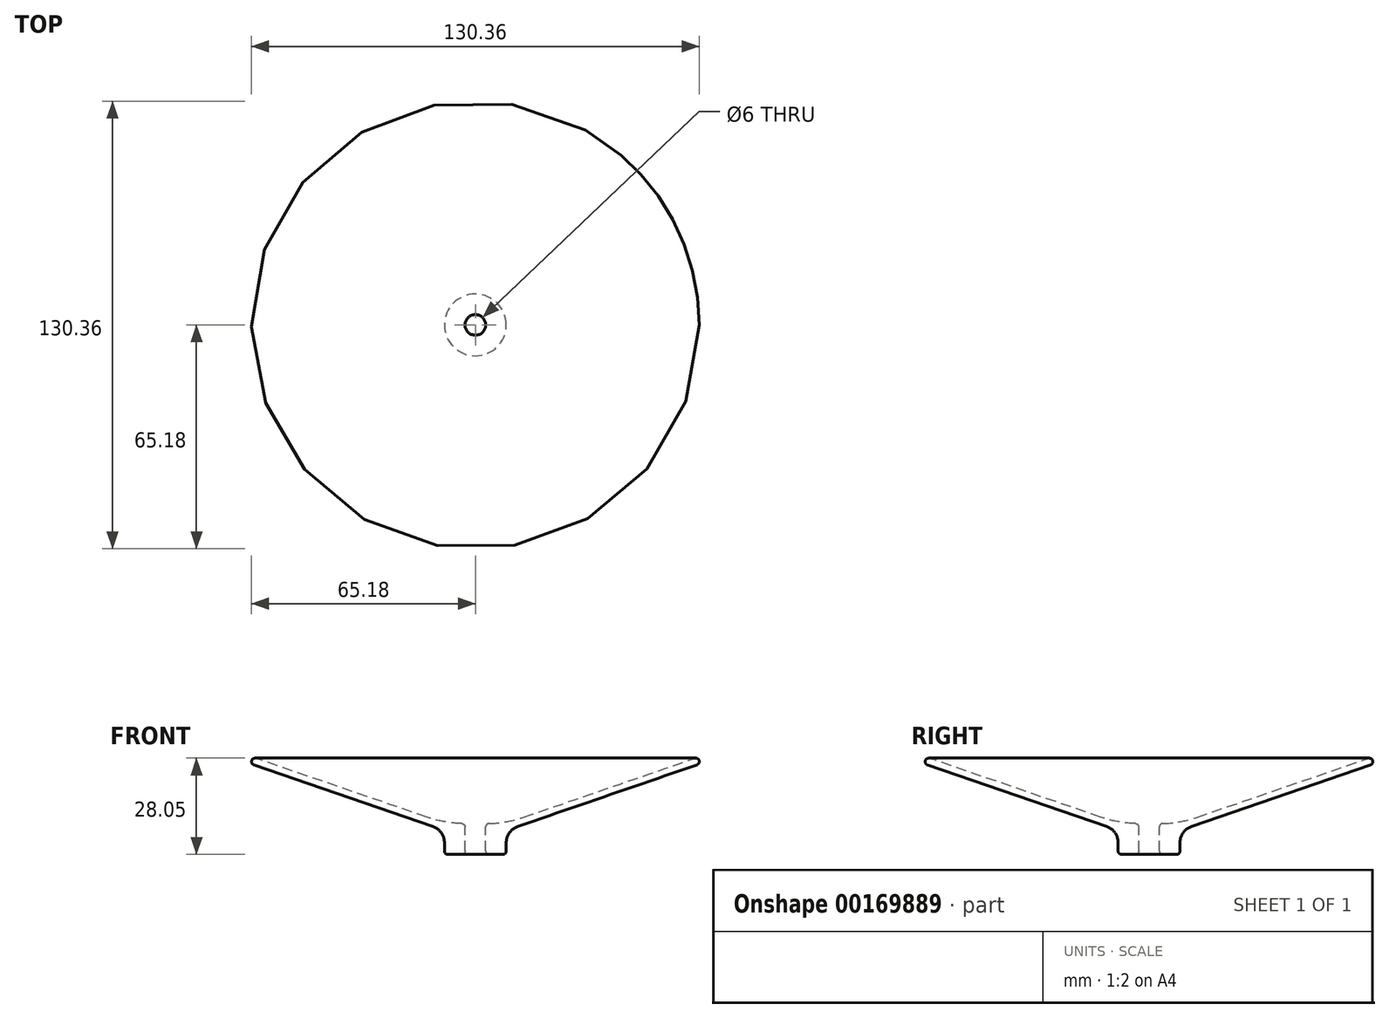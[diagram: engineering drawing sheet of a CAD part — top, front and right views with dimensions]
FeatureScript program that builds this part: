
annotation { "Feature Type Name" : "Feature", "Feature Type Description" : "" }
export const myFeature = defineFeature(function(context is Context, id is Id, definition is map)
    precondition{}
    {
        {
            var Q0;
            Q0=qCreatedBy(makeId("Right.planeOp"),FACE);
            var sketch = newSketch(context, id + "F0", { "sketchPlane" : qUnion([Q0])});
            skLineSegment(sketch, "E0", {"start": v(0, 28) * mm, "end": v(0, 0) * mm, "construction": true});
            skLineSegment(sketch, "E1", {"start": v(0, 0) * mm, "end": v(-9, 0) * mm, "construction": true});
            skLineSegment(sketch, "E2", {"start": v(0, 28) * mm, "end": v(-70, 28) * mm, "construction": true});
            skLineSegment(sketch, "E3", {"start": v(0, 3.93) * mm, "end": v(-3, 3.93) * mm, "construction": true});
            skLineSegment(sketch, "E4", {"start": v(-64.5, 26.1) * mm, "end": v(-12.37, 8.16) * mm});
            skLineSegment(sketch, "E5", {"start": v(-9, 3.43) * mm, "end": v(-9, 1) * mm});
            skLineSegment(sketch, "E6", {"start": v(-3, 1) * mm, "end": v(-3, 7.05) * mm});
            skLineSegment(sketch, "E7", {"start": v(-14.07, 10.86) * mm, "end": v(-63.86, 28) * mm});
            skPoint(sketch, "E8.visualSharp", {"position": v(-9, 7) * mm});
            skArc(sketch, "E8.filletArc", {"start": v(-9, 3.43) * mm, "mid": v(-9.93, 6.34) * mm, "end": v(-12.37, 8.16) * mm});
            skLineSegment(sketch, "E9", {"start": v(-8, 0) * mm, "end": v(-4, 0) * mm});
            skPoint(sketch, "E10.visualSharp", {"position": v(-9, 0) * mm});
            skArc(sketch, "E10.filletArc", {"start": v(-9, 1) * mm, "mid": v(-8.7, 0.3) * mm, "end": v(-8, 0) * mm});
            skPoint(sketch, "E11.visualSharp", {"position": v(-3, 0) * mm});
            skArc(sketch, "E11.filletArc", {"start": v(-4, 0) * mm, "mid": v(-3.3, 0.3) * mm, "end": v(-3, 1) * mm});
            skPoint(sketch, "E12", {"position": v(-14.07, 10.86) * mm});
            skLineSegment(sketch, "E13", {"start": v(-3, 7.05) * mm, "end": v(-3, 8.02) * mm});
            skArc(sketch, "E14", {"start": v(-14.07, 10.86) * mm, "mid": v(-9.1, 9.56) * mm, "end": v(-3.97, 9.02) * mm});
            skPoint(sketch, "E15.visualSharp", {"position": v(-3, 9) * mm});
            skArc(sketch, "E15.filletArc", {"start": v(-3, 8.02) * mm, "mid": v(-3.28, 8.71) * mm, "end": v(-3.97, 9.02) * mm});
            skLineSegment(sketch, "E16", {"start": v(-63.86, 28) * mm, "end": v(-63.86, 28) * mm});
            skPoint(sketch, "E17.visualSharp", {"position": v(-70, 28) * mm});
            skArc(sketch, "E17.filletArc", {"start": v(-63.86, 28) * mm, "mid": v(-65.13, 27.38) * mm, "end": v(-64.5, 26.1) * mm});
            skSolve(sketch);
        }
        {
            var Q0;
            Q0=makeQuery(id+"F0.imprint","IMPRINT",FACE,{"disambiguationData":[TD([[makeQuery(id+"F0.imprint","IMPRINT",EDGE,{"derivedFrom":sQuery(id+"F0.wireOp",EDGE,"E4")}),1.0]])]});
            var Q1;
            Q1=sQuery(id+"F0.wireOp",EDGE,"E0");
            revolve(context, id + "F1", {"entities" : qUnion([Q0]), "axis" : qUnion([Q1]), "revolveType" : RevolveType.FULL});
        }
    });
